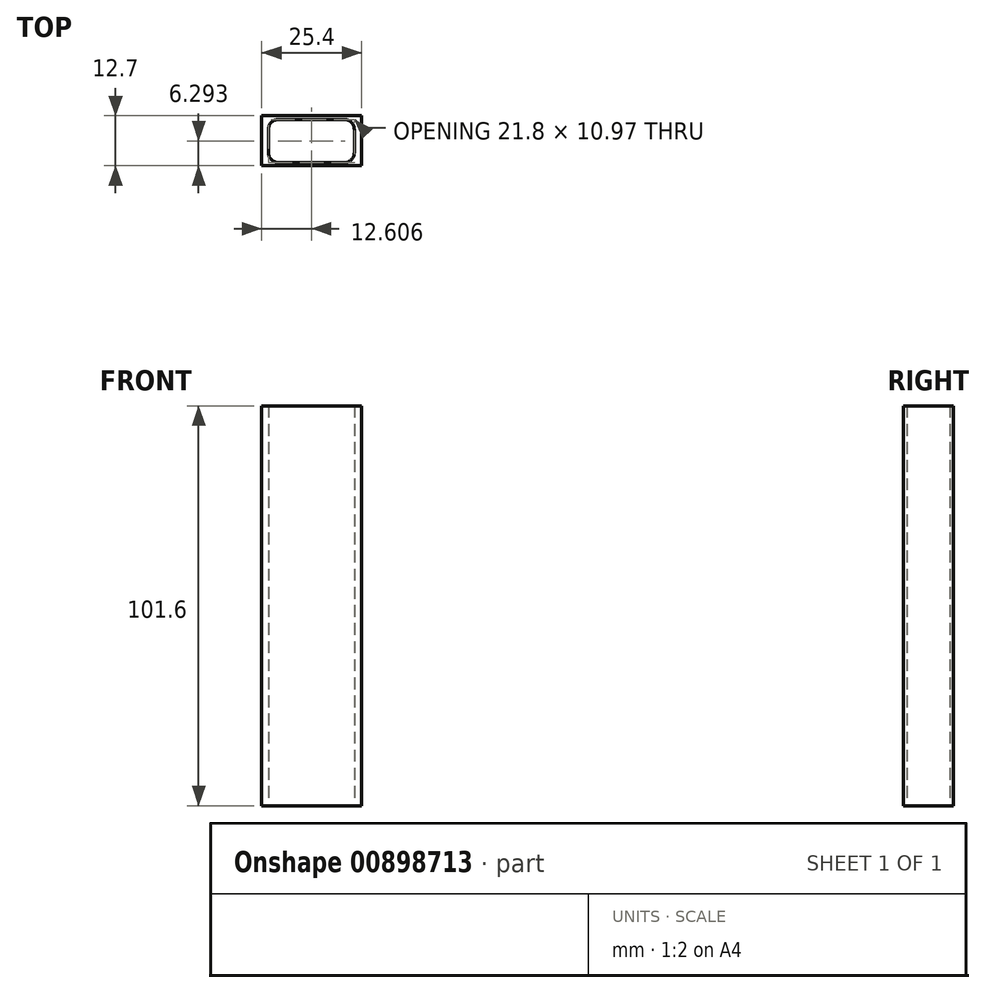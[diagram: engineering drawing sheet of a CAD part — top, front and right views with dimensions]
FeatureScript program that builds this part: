
annotation { "Feature Type Name" : "Feature", "Feature Type Description" : "" }
export const myFeature = defineFeature(function(context is Context, id is Id, definition is map)
    precondition{}
    {
        {
            var Q0;
            Q0=qCreatedBy(makeId("Top.planeOp"),FACE);
            var sketch = newSketch(context, id + "F0", { "sketchPlane" : qUnion([Q0])});
            skLineSegment(sketch, "E0", {"start": v(-12.7, 4.51) * mm, "end": v(-12.7, 6.35) * mm, "construction": true});
            skLineSegment(sketch, "E1", {"start": v(12.7, 0) * mm, "end": v(12.7, -6.35) * mm, "construction": true});
            skLineSegment(sketch, "E2.bottom", {"start": v(-12.7, 6.35) * mm, "end": v(12.7, 6.35) * mm});
            skLineSegment(sketch, "E2.top", {"start": v(-12.7, -6.35) * mm, "end": v(12.7, -6.35) * mm});
            skLineSegment(sketch, "E2.left", {"start": v(-12.7, 6.35) * mm, "end": v(-12.7, -6.35) * mm});
            skLineSegment(sketch, "E2.right", {"start": v(12.7, 6.35) * mm, "end": v(12.7, -6.35) * mm});
            skPoint(sketch, "E3.firstSnap0", {"position": v(-12.7, 5.43) * mm});
            skPoint(sketch, "E3.oppositeSnap0", {"position": v(12.7, -3.18) * mm});
            skLineSegment(sketch, "E4.bottom", {"start": v(-11, 5.43) * mm, "end": v(10.8, 5.43) * mm});
            skLineSegment(sketch, "E4.top", {"start": v(-11, -5.54) * mm, "end": v(10.8, -5.54) * mm});
            skLineSegment(sketch, "E4.left", {"start": v(-11, 5.43) * mm, "end": v(-11, -5.54) * mm});
            skLineSegment(sketch, "E4.right", {"start": v(10.8, 5.43) * mm, "end": v(10.8, -5.54) * mm});
            skSolve(sketch);
        }
        {
            var Q0;
            Q0 = qSketchRegion(id + "F0", true);
            extrude(context, id + "F1", {"entities" : qUnion([Q0]), "depth" : 101.6 * mm, "offsetDistance" : 25.4 * mm});
        }
        {
            var Q0;
            Q0=makeQuery(id+"F1.opExtrude","SWEPT_EDGE",EDGE,{"disambiguationData":[OSD([sQuery(id+"F0.wireOp",EDGE,"E4.top"),sQuery(id+"F0.wireOp",EDGE,"E4.left")])]});
            var Q1;
            Q1=makeQuery(id+"F1.opExtrude","SWEPT_EDGE",EDGE,{"disambiguationData":[OSD([sQuery(id+"F0.wireOp",EDGE,"E4.top"),sQuery(id+"F0.wireOp",EDGE,"E4.right")])]});
            var Q2;
            Q2=makeQuery(id+"F1.opExtrude","SWEPT_EDGE",EDGE,{"disambiguationData":[OSD([sQuery(id+"F0.wireOp",EDGE,"E4.bottom"),sQuery(id+"F0.wireOp",EDGE,"E4.right")])]});
            var Q3;
            Q3=makeQuery(id+"F1.opExtrude","SWEPT_EDGE",EDGE,{"disambiguationData":[OSD([sQuery(id+"F0.wireOp",EDGE,"E4.bottom"),sQuery(id+"F0.wireOp",EDGE,"E4.left")])]});
            fillet(context, id + "F2", {"entities" : qUnion([Q0, Q1, Q2, Q3]), "radius" : 2.54 * mm, "tangentPropagation" : true, "allowEdgeOverflow" : false});
        }
    });
